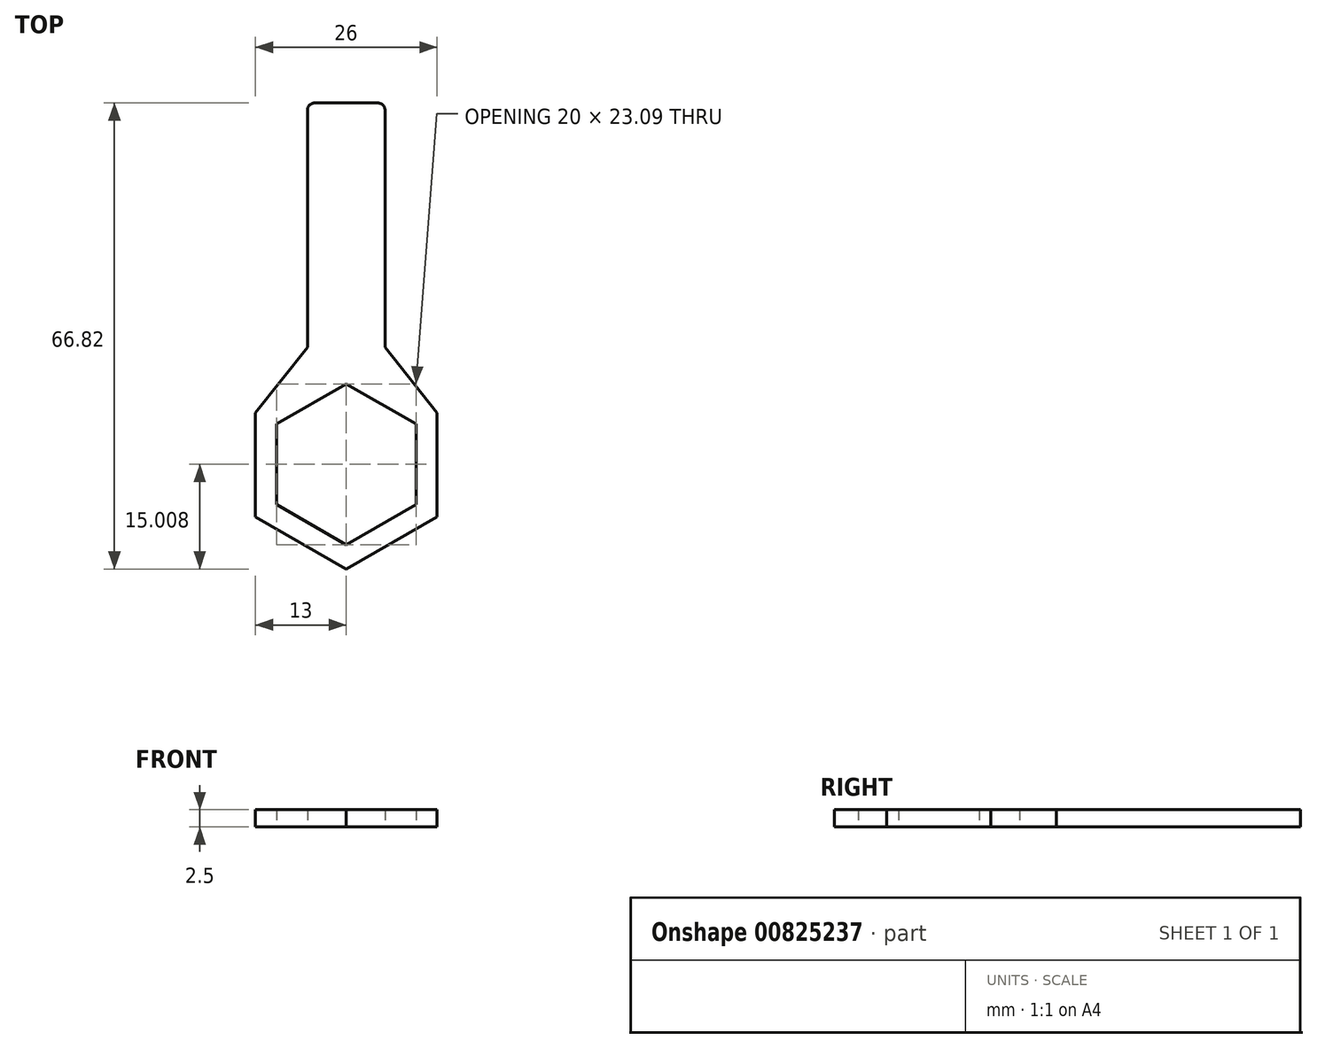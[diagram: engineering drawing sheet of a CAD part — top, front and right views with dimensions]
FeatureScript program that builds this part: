
annotation { "Feature Type Name" : "Feature", "Feature Type Description" : "" }
export const myFeature = defineFeature(function(context is Context, id is Id, definition is map)
    precondition{}
    {
        {
            var Q0;
            Q0=qCreatedBy(makeId("Top.planeOp"),FACE);
            var sketch = newSketch(context, id + "F0", { "sketchPlane" : qUnion([Q0])});
            skLineSegment(sketch, "E0", {"start": v(-5.55, 0) * mm, "end": v(-5.55, 35) * mm});
            skLineSegment(sketch, "E1", {"start": v(-5.55, 35) * mm, "end": v(5.55, 35) * mm});
            skLineSegment(sketch, "E2", {"start": v(5.55, 35) * mm, "end": v(5.55, 0) * mm});
            skLineSegment(sketch, "E3", {"start": v(0, 35) * mm, "end": v(0, -31.82) * mm, "construction": true});
            skLineSegment(sketch, "E4", {"start": v(5.55, 0) * mm, "end": v(13, -9.4) * mm});
            skLineSegment(sketch, "E5", {"start": v(13, -9.4) * mm, "end": v(13, -24.32) * mm});
            skLineSegment(sketch, "E6", {"start": v(13, -24.32) * mm, "end": v(0, -31.82) * mm});
            skLineSegment(sketch, "E7.MirrorCS", {"start": v(-13, -24.32) * mm, "end": v(0, -31.82) * mm});
            skLineSegment(sketch, "E8.MirrorCS", {"start": v(-13, -9.4) * mm, "end": v(-13, -24.32) * mm});
            skLineSegment(sketch, "E9.MirrorCS", {"start": v(-5.55, 0) * mm, "end": v(-13, -9.4) * mm});
            skCircle(sketch, "E10.cCircle", {"center": v(0, -16.81) * mm, "radius": 10 * mm, "construction": true});
            skLineSegment(sketch, "E10.0", {"start": v(10, -22.59) * mm, "end": v(0, -28.36) * mm});
            skLineSegment(sketch, "E10.1", {"start": v(0, -28.36) * mm, "end": v(-10, -22.59) * mm});
            skLineSegment(sketch, "E10.2", {"start": v(-10, -22.59) * mm, "end": v(-10, -11.04) * mm});
            skLineSegment(sketch, "E10.3", {"start": v(-10, -11.04) * mm, "end": v(0, -5.26) * mm});
            skLineSegment(sketch, "E10.4", {"start": v(0, -5.26) * mm, "end": v(10, -11.04) * mm});
            skLineSegment(sketch, "E10.5", {"start": v(10, -11.04) * mm, "end": v(10, -22.59) * mm});
            skPoint(sketch, "E10.0.midPoint", {"position": v(5, -25.47) * mm});
            skSolve(sketch);
        }
        {
            var Q0;
            Q0 = qSketchRegion(id + "F0", true);
            extrude(context, id + "F1", {"entities" : qUnion([Q0]), "depth" : 2.5 * mm, "offsetDistance" : 25 * mm});
        }
        {
            var Q0;
            Q0=makeQuery(id+"F1.opExtrude","SWEPT_EDGE",EDGE,{"disambiguationData":[OSD([sQuery(id+"F0.wireOp",EDGE,"E0"),sQuery(id+"F0.wireOp",EDGE,"E1")])]});
            var Q1;
            Q1=makeQuery(id+"F1.opExtrude","SWEPT_EDGE",EDGE,{"disambiguationData":[OSD([sQuery(id+"F0.wireOp",EDGE,"E1"),sQuery(id+"F0.wireOp",EDGE,"E2")])]});
            fillet(context, id + "F2", {"entities" : qUnion([Q0, Q1]), "radius" : 1 * mm, "tangentPropagation" : true, "allowEdgeOverflow" : false});
        }
    });
